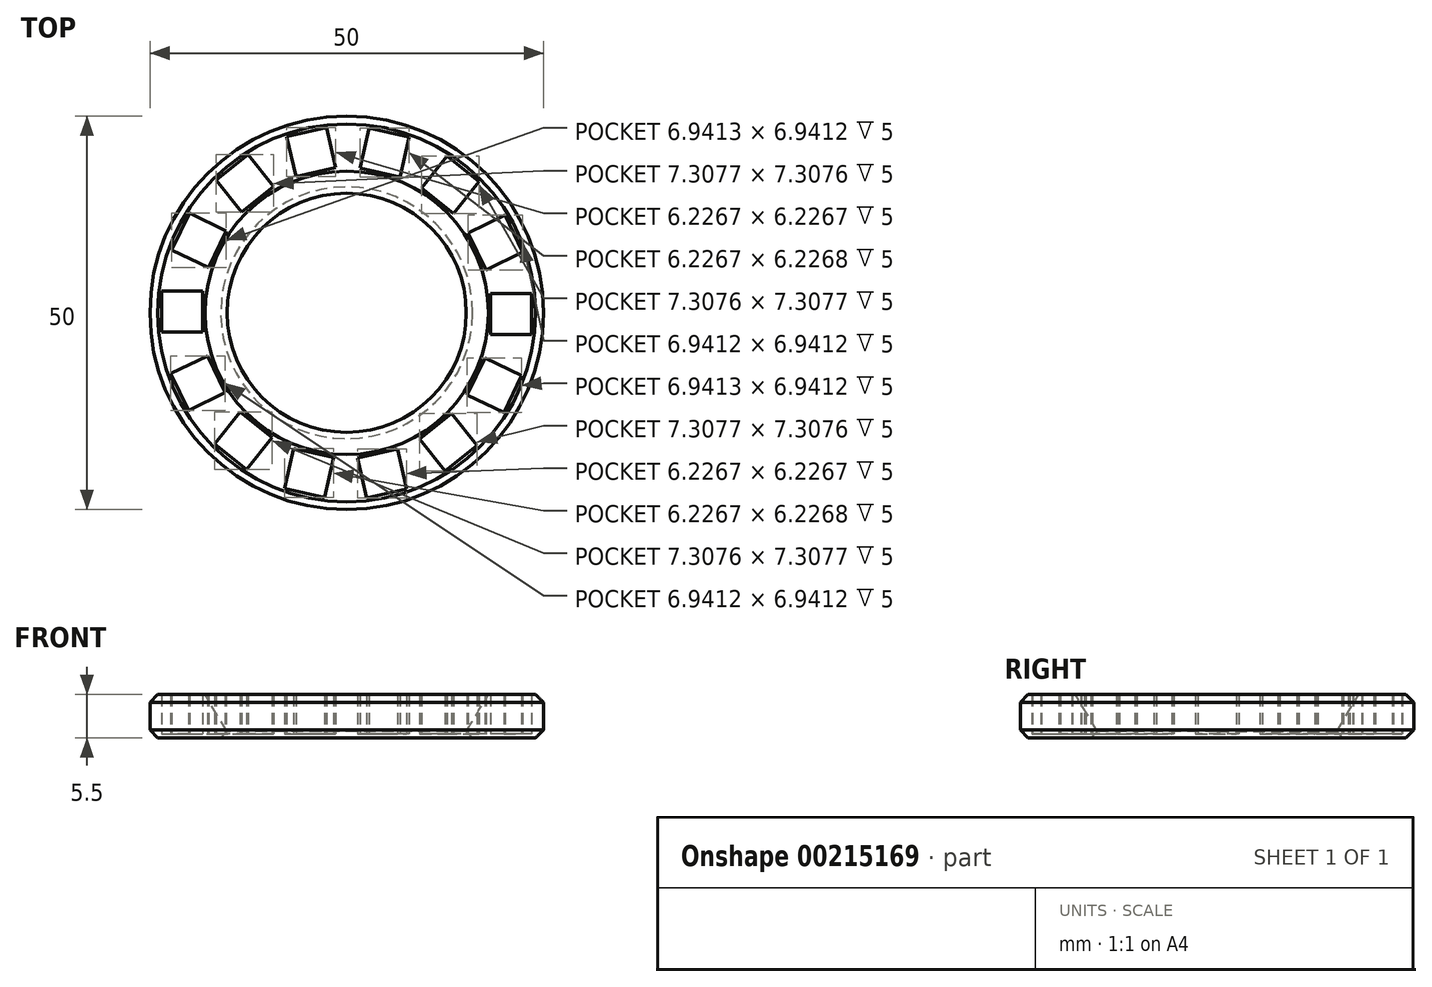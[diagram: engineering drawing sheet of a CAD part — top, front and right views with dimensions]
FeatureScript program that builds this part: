
annotation { "Feature Type Name" : "Feature", "Feature Type Description" : "" }
export const myFeature = defineFeature(function(context is Context, id is Id, definition is map)
    precondition{}
    {
        {
            var Q0;
            Q0=qCreatedBy(makeId("Top.planeOp"),FACE);
            var sketch = newSketch(context, id + "F0", { "sketchPlane" : qUnion([Q0])});
            skCircle(sketch, "E0", {"center": v(0, 0) * mm, "radius": 25 * mm});
            skCircle(sketch, "E1", {"center": v(0, 0) * mm, "radius": 15 * mm});
            skLineSegment(sketch, "E2.bottom", {"start": v(-23.5, 2.75) * mm, "end": v(-18.3, 2.75) * mm});
            skLineSegment(sketch, "E2.top", {"start": v(-23.5, -2.45) * mm, "end": v(-18.3, -2.45) * mm});
            skLineSegment(sketch, "E2.left", {"start": v(-23.5, 2.75) * mm, "end": v(-23.5, -2.45) * mm});
            skLineSegment(sketch, "E2.right", {"start": v(-18.3, 2.75) * mm, "end": v(-18.3, -2.45) * mm});
            skLineSegment(sketch, "E3.1.0", {"start": v(-19.98, 12.67) * mm, "end": v(-22.24, 7.99) * mm});
            skLineSegment(sketch, "E3.1.1", {"start": v(-19.98, 12.67) * mm, "end": v(-15.3, 10.42) * mm});
            skLineSegment(sketch, "E3.1.2", {"start": v(-15.3, 10.42) * mm, "end": v(-17.55, 5.73) * mm});
            skLineSegment(sketch, "E3.1.3", {"start": v(-22.24, 7.99) * mm, "end": v(-17.55, 5.73) * mm});
            skLineSegment(sketch, "E3.2.0", {"start": v(-12.5, 20.09) * mm, "end": v(-16.57, 16.85) * mm});
            skLineSegment(sketch, "E3.2.1", {"start": v(-12.5, 20.09) * mm, "end": v(-9.26, 16.02) * mm});
            skLineSegment(sketch, "E3.2.2", {"start": v(-9.26, 16.02) * mm, "end": v(-13.33, 12.78) * mm});
            skLineSegment(sketch, "E3.2.3", {"start": v(-16.57, 16.85) * mm, "end": v(-13.33, 12.78) * mm});
            skLineSegment(sketch, "E3.3.0", {"start": v(-2.55, 23.52) * mm, "end": v(-7.62, 22.37) * mm});
            skLineSegment(sketch, "E3.3.1", {"start": v(-2.55, 23.52) * mm, "end": v(-1.4, 18.45) * mm});
            skLineSegment(sketch, "E3.3.2", {"start": v(-1.4, 18.45) * mm, "end": v(-6.46, 17.3) * mm});
            skLineSegment(sketch, "E3.3.3", {"start": v(-7.62, 22.37) * mm, "end": v(-6.46, 17.3) * mm});
            skLineSegment(sketch, "E3.4.0", {"start": v(7.91, 22.3) * mm, "end": v(2.84, 23.46) * mm});
            skLineSegment(sketch, "E3.4.1", {"start": v(7.91, 22.3) * mm, "end": v(6.75, 17.23) * mm});
            skLineSegment(sketch, "E3.4.2", {"start": v(6.75, 17.23) * mm, "end": v(1.68, 18.39) * mm});
            skLineSegment(sketch, "E3.4.3", {"start": v(2.84, 23.46) * mm, "end": v(1.68, 18.39) * mm});
            skLineSegment(sketch, "E3.5.0", {"start": v(16.8, 16.66) * mm, "end": v(12.74, 19.9) * mm});
            skLineSegment(sketch, "E3.5.1", {"start": v(16.8, 16.66) * mm, "end": v(13.56, 12.6) * mm});
            skLineSegment(sketch, "E3.5.2", {"start": v(13.56, 12.6) * mm, "end": v(9.5, 15.84) * mm});
            skLineSegment(sketch, "E3.5.3", {"start": v(12.74, 19.9) * mm, "end": v(9.5, 15.84) * mm});
            skLineSegment(sketch, "E3.6.0", {"start": v(22.37, 7.72) * mm, "end": v(20.1, 12.4) * mm});
            skLineSegment(sketch, "E3.6.1", {"start": v(22.37, 7.72) * mm, "end": v(17.68, 5.46) * mm});
            skLineSegment(sketch, "E3.6.2", {"start": v(17.68, 5.46) * mm, "end": v(15.42, 10.15) * mm});
            skLineSegment(sketch, "E3.6.3", {"start": v(20.1, 12.4) * mm, "end": v(15.42, 10.15) * mm});
            skLineSegment(sketch, "E3.7.0", {"start": v(23.5, -2.75) * mm, "end": v(23.5, 2.45) * mm});
            skLineSegment(sketch, "E3.7.1", {"start": v(23.5, -2.75) * mm, "end": v(18.3, -2.75) * mm});
            skLineSegment(sketch, "E3.7.2", {"start": v(18.3, -2.75) * mm, "end": v(18.3, 2.45) * mm});
            skLineSegment(sketch, "E3.7.3", {"start": v(23.5, 2.45) * mm, "end": v(18.3, 2.45) * mm});
            skLineSegment(sketch, "E3.anchor1", {"start": v(0, 0) * mm, "end": v(-23.5, -2.45) * mm, "construction": true});
            skLineSegment(sketch, "E3.anchor2", {"start": v(0, 0) * mm, "end": v(-20.1, -12.4) * mm, "construction": true});
            skLineSegment(sketch, "E4.2.8.0", {"start": v(19.98, -12.67) * mm, "end": v(22.24, -7.99) * mm});
            skLineSegment(sketch, "E4.3.8.0", {"start": v(19.98, -12.67) * mm, "end": v(15.3, -10.42) * mm});
            skLineSegment(sketch, "E4.6.8.0", {"start": v(15.3, -10.42) * mm, "end": v(17.55, -5.73) * mm});
            skLineSegment(sketch, "E4.9.8.0", {"start": v(22.24, -7.99) * mm, "end": v(17.55, -5.73) * mm});
            skLineSegment(sketch, "E4.2.9.0", {"start": v(12.5, -20.09) * mm, "end": v(16.57, -16.85) * mm});
            skLineSegment(sketch, "E4.3.9.0", {"start": v(12.5, -20.09) * mm, "end": v(9.26, -16.02) * mm});
            skLineSegment(sketch, "E4.6.9.0", {"start": v(9.26, -16.02) * mm, "end": v(13.33, -12.78) * mm});
            skLineSegment(sketch, "E4.9.9.0", {"start": v(16.57, -16.85) * mm, "end": v(13.33, -12.78) * mm});
            skLineSegment(sketch, "E5.2.10.0", {"start": v(2.55, -23.52) * mm, "end": v(7.62, -22.37) * mm});
            skLineSegment(sketch, "E5.3.10.0", {"start": v(2.55, -23.52) * mm, "end": v(1.4, -18.45) * mm});
            skLineSegment(sketch, "E5.6.10.0", {"start": v(1.4, -18.45) * mm, "end": v(6.46, -17.3) * mm});
            skLineSegment(sketch, "E5.9.10.0", {"start": v(7.62, -22.37) * mm, "end": v(6.46, -17.3) * mm});
            skLineSegment(sketch, "E5.2.11.0", {"start": v(-7.91, -22.3) * mm, "end": v(-2.84, -23.46) * mm});
            skLineSegment(sketch, "E5.3.11.0", {"start": v(-7.91, -22.3) * mm, "end": v(-6.75, -17.23) * mm});
            skLineSegment(sketch, "E5.6.11.0", {"start": v(-6.75, -17.23) * mm, "end": v(-1.68, -18.39) * mm});
            skLineSegment(sketch, "E5.9.11.0", {"start": v(-2.84, -23.46) * mm, "end": v(-1.68, -18.39) * mm});
            skLineSegment(sketch, "E5.2.12.0", {"start": v(-16.8, -16.66) * mm, "end": v(-12.74, -19.9) * mm});
            skLineSegment(sketch, "E5.3.12.0", {"start": v(-16.8, -16.66) * mm, "end": v(-13.56, -12.6) * mm});
            skLineSegment(sketch, "E5.6.12.0", {"start": v(-13.56, -12.6) * mm, "end": v(-9.5, -15.84) * mm});
            skLineSegment(sketch, "E5.9.12.0", {"start": v(-12.74, -19.9) * mm, "end": v(-9.5, -15.84) * mm});
            skLineSegment(sketch, "E5.2.13.0", {"start": v(-22.37, -7.72) * mm, "end": v(-20.1, -12.4) * mm});
            skLineSegment(sketch, "E5.3.13.0", {"start": v(-22.37, -7.72) * mm, "end": v(-17.68, -5.46) * mm});
            skLineSegment(sketch, "E5.6.13.0", {"start": v(-17.68, -5.46) * mm, "end": v(-15.42, -10.15) * mm});
            skLineSegment(sketch, "E5.9.13.0", {"start": v(-20.1, -12.4) * mm, "end": v(-15.42, -10.15) * mm});
            skSolve(sketch);
        }
        {
            var Q0;
            Q0=makeQuery(id+"F0.imprint","IMPRINT",FACE,{"disambiguationData":[TD([[makeQuery(id+"F0.imprint","IMPRINT",EDGE,{"derivedFrom":sQuery(id+"F0.wireOp",EDGE,"E0")}),1.0]])]});
            extrude(context, id + "F1", {"entities" : qUnion([Q0]), "depth" : 5 * mm});
        }
        {
            var Q0;
            Q0=makeQuery(id+"F0.imprint","IMPRINT",FACE,{"disambiguationData":[TD([[makeQuery(id+"F0.imprint","IMPRINT",EDGE,{"derivedFrom":sQuery(id+"F0.wireOp",EDGE,"E3.1.0")}),1.0]])]});
            var Q1;
            Q1=makeQuery(id+"F0.imprint","IMPRINT",FACE,{"disambiguationData":[TD([[makeQuery(id+"F0.imprint","IMPRINT",EDGE,{"derivedFrom":sQuery(id+"F0.wireOp",EDGE,"E0")}),1.0]])]});
            var Q2;
            Q2=makeQuery(id+"F0.imprint","IMPRINT",FACE,{"disambiguationData":[TD([[makeQuery(id+"F0.imprint","IMPRINT",EDGE,{"derivedFrom":sQuery(id+"F0.wireOp",EDGE,"E3.2.0")}),1.0]])]});
            var Q3;
            Q3=makeQuery(id+"F0.imprint","IMPRINT",FACE,{"disambiguationData":[TD([[makeQuery(id+"F0.imprint","IMPRINT",EDGE,{"derivedFrom":sQuery(id+"F0.wireOp",EDGE,"E3.3.0")}),1.0]])]});
            var Q4;
            Q4=makeQuery(id+"F0.imprint","IMPRINT",FACE,{"disambiguationData":[TD([[makeQuery(id+"F0.imprint","IMPRINT",EDGE,{"derivedFrom":sQuery(id+"F0.wireOp",EDGE,"E3.4.0")}),1.0]])]});
            var Q5;
            Q5=makeQuery(id+"F0.imprint","IMPRINT",FACE,{"disambiguationData":[TD([[makeQuery(id+"F0.imprint","IMPRINT",EDGE,{"derivedFrom":sQuery(id+"F0.wireOp",EDGE,"E3.5.0")}),1.0]])]});
            var Q6;
            Q6=makeQuery(id+"F0.imprint","IMPRINT",FACE,{"disambiguationData":[TD([[makeQuery(id+"F0.imprint","IMPRINT",EDGE,{"derivedFrom":sQuery(id+"F0.wireOp",EDGE,"E3.6.0")}),1.0]])]});
            var Q7;
            Q7=makeQuery(id+"F0.imprint","IMPRINT",FACE,{"disambiguationData":[TD([[makeQuery(id+"F0.imprint","IMPRINT",EDGE,{"derivedFrom":sQuery(id+"F0.wireOp",EDGE,"E3.7.0")}),1.0]])]});
            var Q8;
            Q8=makeQuery(id+"F0.imprint","IMPRINT",FACE,{"disambiguationData":[TD([[makeQuery(id+"F0.imprint","IMPRINT",EDGE,{"derivedFrom":sQuery(id+"F0.wireOp",EDGE,"E4.2.8.0")}),1.0]])]});
            var Q9;
            Q9=makeQuery(id+"F0.imprint","IMPRINT",FACE,{"disambiguationData":[TD([[makeQuery(id+"F0.imprint","IMPRINT",EDGE,{"derivedFrom":sQuery(id+"F0.wireOp",EDGE,"E4.2.9.0")}),1.0]])]});
            var Q10;
            Q10=makeQuery(id+"F0.imprint","IMPRINT",FACE,{"disambiguationData":[TD([[makeQuery(id+"F0.imprint","IMPRINT",EDGE,{"derivedFrom":sQuery(id+"F0.wireOp",EDGE,"E2.bottom")}),-1.0]])]});
            var Q11;
            Q11=makeQuery(id+"F0.imprint","IMPRINT",FACE,{"disambiguationData":[TD([[makeQuery(id+"F0.imprint","IMPRINT",EDGE,{"derivedFrom":sQuery(id+"F0.wireOp",EDGE,"E5.2.12.0")}),1.0]])]});
            var Q12;
            Q12=makeQuery(id+"F0.imprint","IMPRINT",FACE,{"disambiguationData":[TD([[makeQuery(id+"F0.imprint","IMPRINT",EDGE,{"derivedFrom":sQuery(id+"F0.wireOp",EDGE,"E5.2.13.0")}),1.0]])]});
            var Q13;
            Q13=makeQuery(id+"F0.imprint","IMPRINT",FACE,{"disambiguationData":[TD([[makeQuery(id+"F0.imprint","IMPRINT",EDGE,{"derivedFrom":sQuery(id+"F0.wireOp",EDGE,"E5.2.11.0")}),1.0]])]});
            var Q14;
            Q14=makeQuery(id+"F0.imprint","IMPRINT",FACE,{"disambiguationData":[TD([[makeQuery(id+"F0.imprint","IMPRINT",EDGE,{"derivedFrom":sQuery(id+"F0.wireOp",EDGE,"E5.2.10.0")}),1.0]])]});
            extrude(context, id + "F2", {"entities" : qUnion([Q0, Q1, Q2, Q3, Q4, Q5, Q6, Q7, Q8, Q9, Q10, Q11, Q12, Q13, Q14]), "operationType" : NewBodyOperationType.ADD, "oppositeDirection" : true, "depth" : 0.5 * mm});
        }
        {
            var Q0;
            Q0=makeQuery(id+"F1.opExtrude","CAP_EDGE",EDGE,{"disambiguationData":[OSD([sQuery(id+"F0.wireOp",EDGE,"E1")])],"isStart":false});
            chamfer(context, id + "F3", {"entities" : qUnion([Q0]), "chamferType" : ChamferType.TWO_OFFSETS, "width1" : 5 * mm, "oppositeDirection" : false, "width2" : 3 * mm, "tangentPropagation" : true});
        }
        {
            var Q0;
            Q0=makeQuery(id+"F1.opExtrude","CAP_EDGE",EDGE,{"disambiguationData":[OSD([sQuery(id+"F0.wireOp",EDGE,"E0")])],"isStart":false});
            var Q1;
            Q1=makeQuery(id+"F2.opExtrude","CAP_EDGE",EDGE,{"disambiguationData":[OSD([sQuery(id+"F0.wireOp",EDGE,"E0")])],"isStart":false});
            var Q2;
            Q2=makeQuery(id+"F2.opExtrude","CAP_EDGE",EDGE,{"disambiguationData":[OSD([sQuery(id+"F0.wireOp",EDGE,"E1")])],"isStart":false});
            chamfer(context, id + "F4", {"entities" : qUnion([Q0, Q1, Q2]), "width" : 1 * mm, "tangentPropagation" : true});
        }
    });
